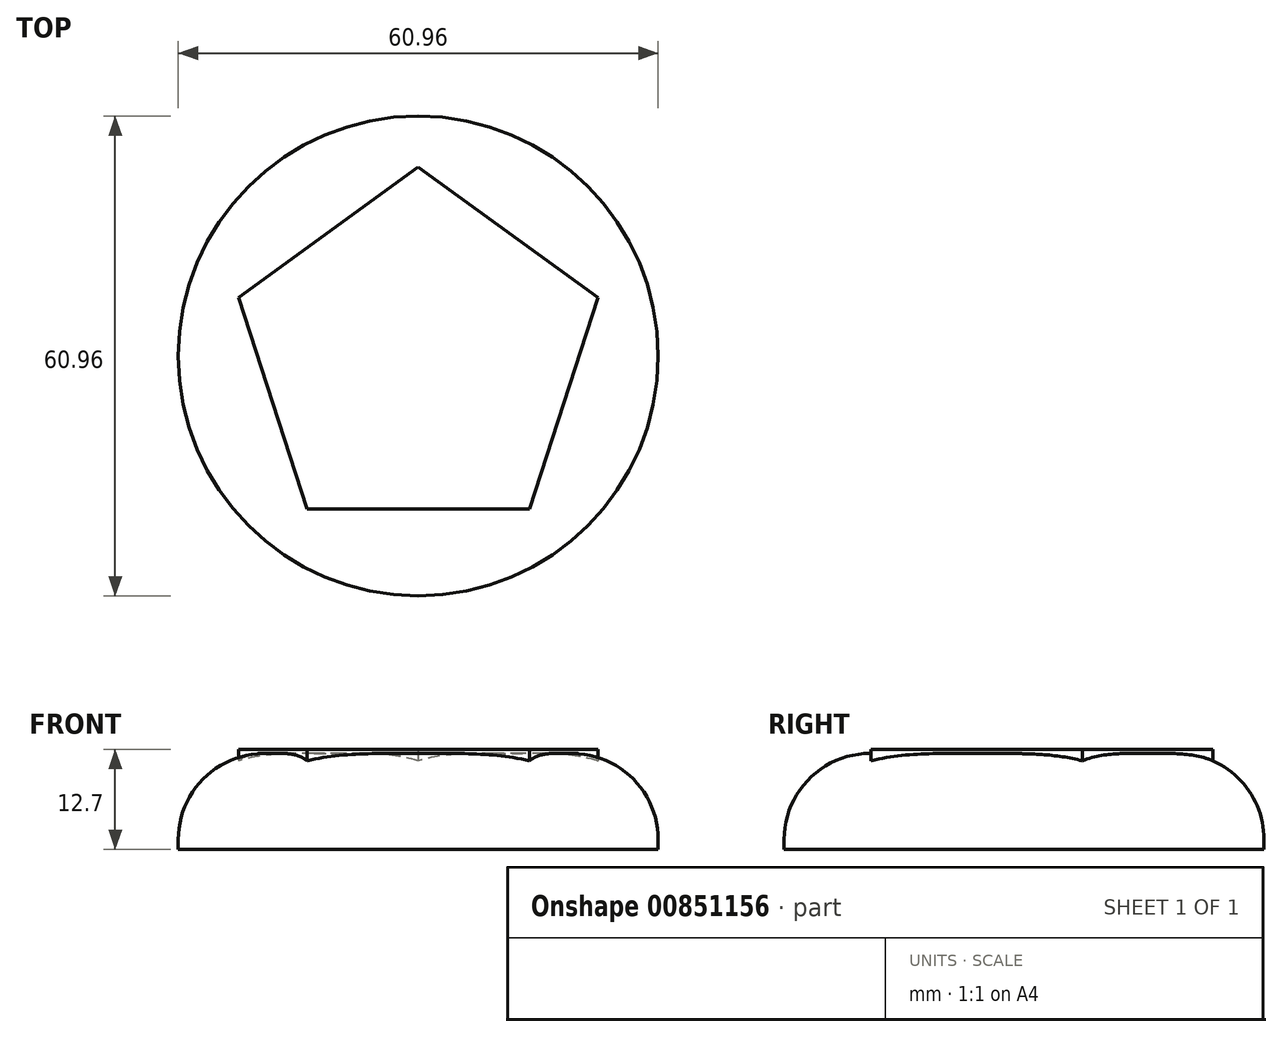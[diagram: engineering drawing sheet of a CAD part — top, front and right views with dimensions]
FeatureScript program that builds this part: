
annotation { "Feature Type Name" : "Feature", "Feature Type Description" : "" }
export const myFeature = defineFeature(function(context is Context, id is Id, definition is map)
    precondition{}
    {
        {
            var Q0;
            Q0=qCreatedBy(makeId("Top.planeOp"),FACE);
            var sketch = newSketch(context, id + "F0", { "sketchPlane" : qUnion([Q0])});
            skCircle(sketch, "E0.cCircle", {"center": v(0, 0) * mm, "radius": 19.43 * mm, "construction": true});
            skLineSegment(sketch, "E0.0", {"start": v(-22.84, 7.42) * mm, "end": v(0, 24.02) * mm});
            skLineSegment(sketch, "E0.1", {"start": v(0, 24.02) * mm, "end": v(22.84, 7.42) * mm});
            skLineSegment(sketch, "E0.2", {"start": v(22.84, 7.42) * mm, "end": v(14.12, -19.43) * mm});
            skLineSegment(sketch, "E0.3", {"start": v(14.12, -19.43) * mm, "end": v(-14.12, -19.43) * mm});
            skLineSegment(sketch, "E0.4", {"start": v(-14.12, -19.43) * mm, "end": v(-22.84, 7.42) * mm});
            skPoint(sketch, "E0.0.midPoint", {"position": v(-11.42, 15.72) * mm});
            skCircle(sketch, "E1", {"center": v(0, 0) * mm, "radius": 30.48 * mm});
            skLineSegment(sketch, "E2", {"start": v(0, 24.02) * mm, "end": v(0, 30.48) * mm});
            skLineSegment(sketch, "E3", {"start": v(-14.12, -19.43) * mm, "end": v(-17.92, -24.66) * mm});
            skLineSegment(sketch, "E4", {"start": v(14.12, -19.43) * mm, "end": v(16.16, -25.84) * mm});
            skLineSegment(sketch, "E5", {"start": v(22.84, 7.42) * mm, "end": v(28.28, 11.37) * mm});
            skLineSegment(sketch, "E6", {"start": v(-22.84, 7.42) * mm, "end": v(-28.27, 11.4) * mm});
            skLineSegment(sketch, "E7", {"start": v(-28.27, 11.4) * mm, "end": v(-22.84, 7.42) * mm});
            skLineSegment(sketch, "E8", {"start": v(0, 30.48) * mm, "end": v(0, 24.02) * mm});
            skLineSegment(sketch, "E9", {"start": v(28.28, 11.37) * mm, "end": v(22.84, 7.42) * mm});
            skLineSegment(sketch, "E10", {"start": v(16.16, -25.84) * mm, "end": v(14.12, -19.43) * mm});
            skLineSegment(sketch, "E11", {"start": v(-17.92, -24.66) * mm, "end": v(-14.12, -19.43) * mm});
            skSolve(sketch);
        }
        {
            var Q0;
            Q0=makeQuery(id+"F0.imprint","IMPRINT",FACE,{"disambiguationData":[TD([[makeQuery(id+"F0.imprint","IMPRINT",EDGE,{"derivedFrom":sQuery(id+"F0.wireOp",EDGE,"E0.0")}),-1.0]])]});
            extrude(context, id + "F1", {"entities" : qUnion([Q0]), "depth" : 12.7 * mm, "offsetDistance" : 25.4 * mm});
        }
        {
            var Q0;
            Q0=makeQuery(id+"F0.imprint","IMPRINT",FACE,{"disambiguationData":[TD([[makeQuery(id+"F0.imprint","IMPRINT",EDGE,{"derivedFrom":sQuery(id+"F0.wireOp",EDGE,"E0.4")}),1.0]])]});
            extrude(context, id + "F2", {"entities" : qUnion([Q0]), "operationType" : NewBodyOperationType.ADD, "depth" : 12.2 * mm, "offsetDistance" : 25.4 * mm});
        }
        {
            var Q0;
            Q0=makeQuery(id+"F0.imprint","IMPRINT",FACE,{"disambiguationData":[TD([[makeQuery(id+"F0.imprint","IMPRINT",EDGE,{"derivedFrom":sQuery(id+"F0.wireOp",EDGE,"E0.0")}),1.0]])]});
            extrude(context, id + "F3", {"entities" : qUnion([Q0]), "operationType" : NewBodyOperationType.ADD, "depth" : 12.2 * mm, "offsetDistance" : 25.4 * mm});
        }
        {
            var Q0;
            Q0=makeQuery(id+"F0.imprint","IMPRINT",FACE,{"disambiguationData":[TD([[makeQuery(id+"F0.imprint","IMPRINT",EDGE,{"derivedFrom":sQuery(id+"F0.wireOp",EDGE,"E0.1")}),1.0]])]});
            extrude(context, id + "F4", {"entities" : qUnion([Q0]), "operationType" : NewBodyOperationType.ADD, "depth" : 12.2 * mm, "offsetDistance" : 25.4 * mm});
        }
        {
            var Q0;
            Q0=makeQuery(id+"F0.imprint","IMPRINT",FACE,{"disambiguationData":[TD([[makeQuery(id+"F0.imprint","IMPRINT",EDGE,{"derivedFrom":sQuery(id+"F0.wireOp",EDGE,"E0.2")}),1.0]])]});
            extrude(context, id + "F5", {"entities" : qUnion([Q0]), "operationType" : NewBodyOperationType.ADD, "depth" : 12.2 * mm, "offsetDistance" : 25.4 * mm});
        }
        {
            var Q0;
            Q0=makeQuery(id+"F0.imprint","IMPRINT",FACE,{"disambiguationData":[TD([[makeQuery(id+"F0.imprint","IMPRINT",EDGE,{"derivedFrom":sQuery(id+"F0.wireOp",EDGE,"E0.3")}),1.0]])]});
            extrude(context, id + "F6", {"entities" : qUnion([Q0]), "operationType" : NewBodyOperationType.ADD, "depth" : 12.2 * mm, "offsetDistance" : 25.4 * mm});
        }
        {
            var Q0;
            {var subQ0=sQuery(id+"F0.wireOp",EDGE,"E1");Q0=makeQuery(id+"F6.boolean.opBoolean","MERGE",EDGE,{"derivedFrom":[makeQuery(id+"F5.boolean.opBoolean","MERGE",EDGE,{"derivedFrom":[makeQuery(id+"F4.boolean.opBoolean","MERGE",EDGE,{"derivedFrom":[makeQuery(id+"F3.boolean.opBoolean","MERGE",EDGE,{"derivedFrom":[makeQuery(id+"F2.opExtrude","CAP_EDGE",EDGE,{"disambiguationData":[OSD([subQ0])],"isStart":false}),makeQuery(id+"F3.opExtrude","CAP_EDGE",EDGE,{"disambiguationData":[OSD([subQ0])],"isStart":false})]}),makeQuery(id+"F4.opExtrude","CAP_EDGE",EDGE,{"disambiguationData":[OSD([subQ0])],"isStart":false})]}),makeQuery(id+"F5.opExtrude","CAP_EDGE",EDGE,{"disambiguationData":[OSD([subQ0])],"isStart":false})]}),makeQuery(id+"F6.opExtrude","CAP_EDGE",EDGE,{"disambiguationData":[OSD([subQ0])],"isStart":false})]});}
            fillet(context, id + "F7", {"entities" : qUnion([Q0]), "radius" : 10.92 * mm, "tangentPropagation" : true, "allowEdgeOverflow" : false});
        }
    });
